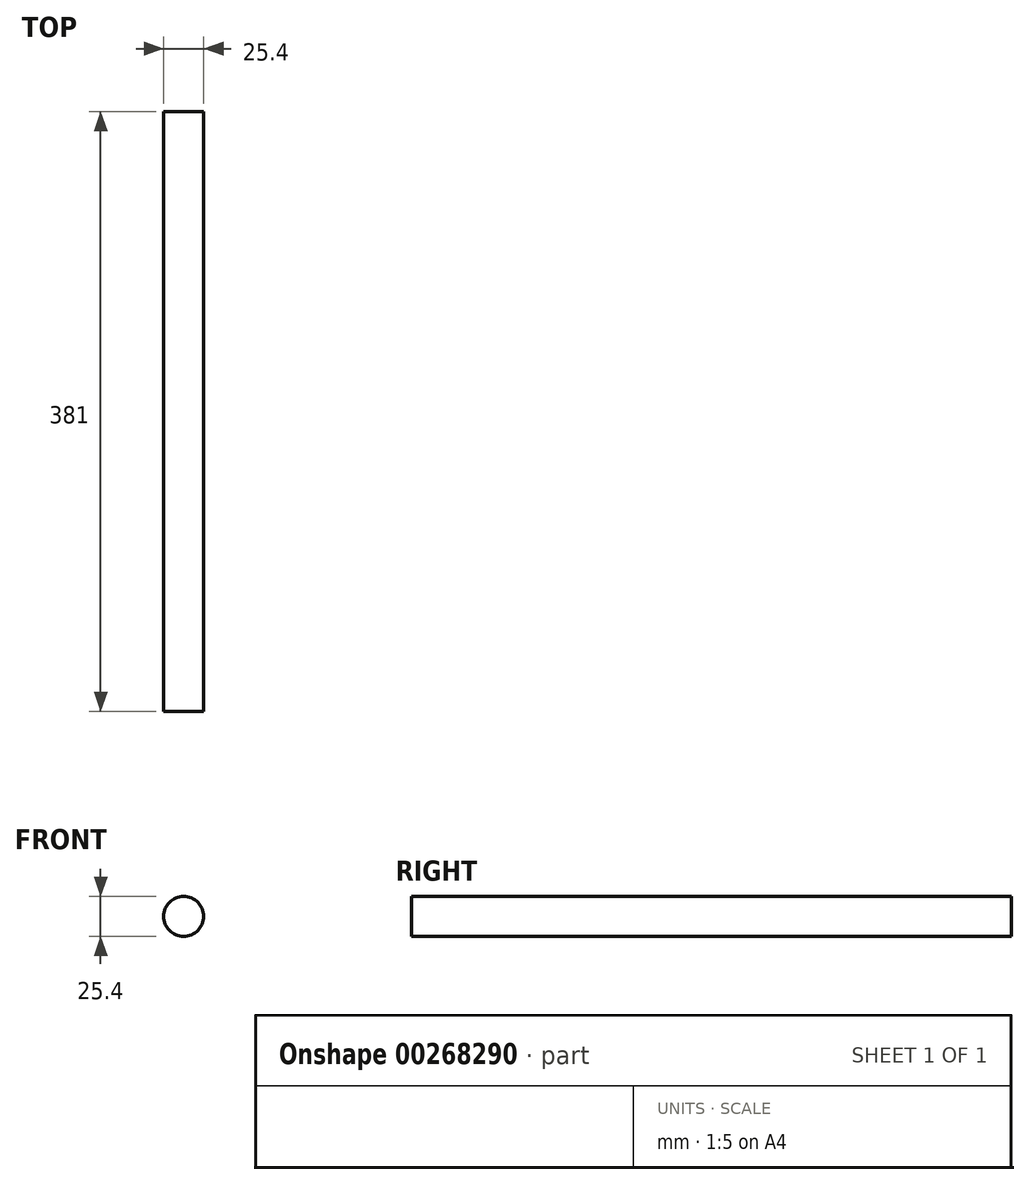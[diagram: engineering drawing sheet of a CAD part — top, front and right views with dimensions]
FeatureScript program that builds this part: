
annotation { "Feature Type Name" : "Feature", "Feature Type Description" : "" }
export const myFeature = defineFeature(function(context is Context, id is Id, definition is map)
    precondition{}
    {
        {
            var Q0;
            Q0=qCreatedBy(makeId("Front.planeOp"),FACE);
            var sketch = newSketch(context, id + "F0", { "sketchPlane" : qUnion([Q0])});
            skCircle(sketch, "E0", {"center": v(0, 0) * mm, "radius": 12.7 * mm});
            skSolve(sketch);
        }
        {
            var Q0;
            Q0=makeQuery(id+"F0.imprint","IMPRINT",FACE,{"disambiguationData":[TD([[makeQuery(id+"F0.imprint","IMPRINT",EDGE,{"derivedFrom":sQuery(id+"F0.wireOp",EDGE,"E0")}),1.0]])]});
            extrude(context, id + "F1", {"entities" : qUnion([Q0]), "depth" : 381 * mm});
        }
    });
